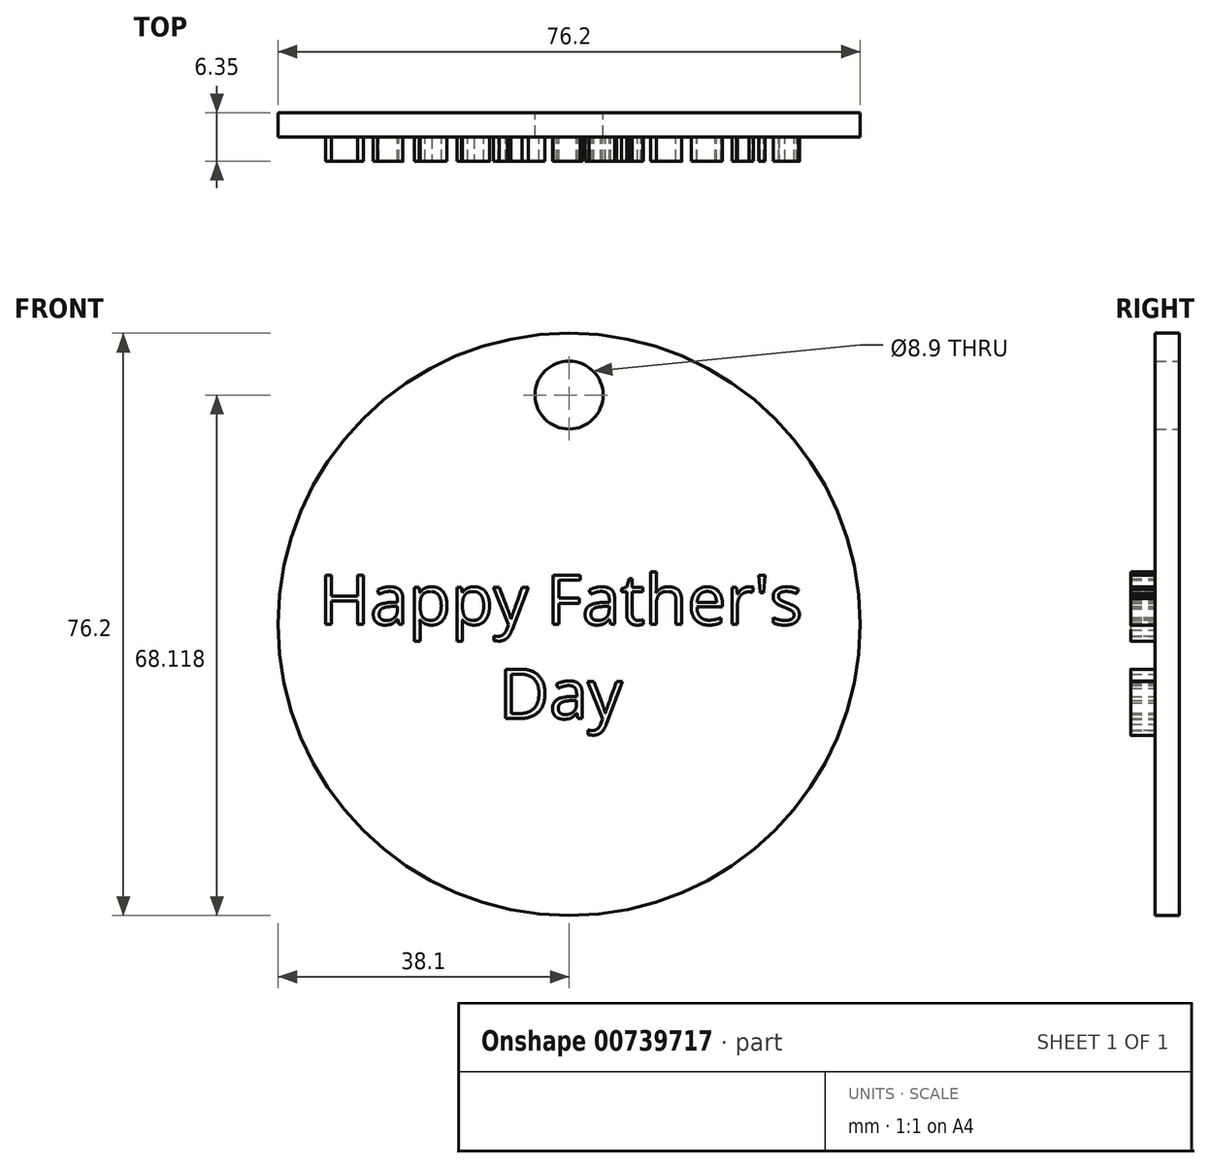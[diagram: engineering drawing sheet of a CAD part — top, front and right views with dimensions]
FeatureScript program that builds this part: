
annotation { "Feature Type Name" : "Feature", "Feature Type Description" : "" }
export const myFeature = defineFeature(function(context is Context, id is Id, definition is map)
    precondition{}
    {
        {
            var Q0;
            Q0=qCreatedBy(makeId("Front.planeOp"),FACE);
            var sketch = newSketch(context, id + "F0", { "sketchPlane" : qUnion([Q0])});
            skCircle(sketch, "E0", {"center": v(0, 0) * mm, "radius": 38.1 * mm});
            skSolve(sketch);
        }
        {
            var Q0;
            Q0 = qSketchRegion(id + "F0", true);
            extrude(context, id + "F1", {"entities" : qUnion([Q0]), "depth" : 3.17 * mm, "offsetDistance" : 25.4 * mm});
        }
        {
            var Q0;
            Q0=makeQuery(id+"F1.opExtrude","CAP_FACE",FACE,{"disambiguationData":[OSD([sQuery(id+"F0.wireOp",EDGE,"E0")])],"isStart":false});
            var sketch = newSketch(context, id + "F2", { "sketchPlane" : qUnion([Q0])});
            skText(sketch, "E1", { "text": "Happy Father\'s\n          Day", "fontName": "OpenSans-Regular.ttf"});
            const initialGuessF2  = {"E1": [-0.03273, 0, 1, 0, 0.00652]};
            skSetInitialGuess(sketch, initialGuessF2);
            skSolve(sketch);
        }
        {
            var Q0;
            Q0 = qSketchRegion(id + "F2", true);
            extrude(context, id + "F3", {"entities" : qUnion([Q0]), "operationType" : NewBodyOperationType.ADD, "depth" : 3.17 * mm, "offsetDistance" : 25.4 * mm});
        }
        {
            var Q0;
            {var subQ0=sQuery(id+"F0.wireOp",EDGE,"E0");Q0=makeQuery(id+"F3.boolean.opBoolean","SPLIT",FACE,{"disambiguationData":[TD([makeQuery(id+"F1.opExtrude","SWEPT_FACE",FACE,{"disambiguationData":[OSD([subQ0])]})])],"derivedFrom":makeQuery(id+"F1.opExtrude","CAP_FACE",FACE,{"disambiguationData":[OSD([subQ0])],"isStart":false})});}
            var sketch = newSketch(context, id + "F4", { "sketchPlane" : qUnion([Q0])});
            skCircle(sketch, "E2", {"center": v(0, 30.02) * mm, "radius": 4.45 * mm});
            skSolve(sketch);
        }
        {
            var Q0;
            Q0 = qSketchRegion(id + "F4", true);
            extrude(context, id + "F5", {"entities" : qUnion([Q0]), "operationType" : NewBodyOperationType.REMOVE, "endBound" : BoundingType.SYMMETRIC, "depth" : 25.4 * mm, "offsetDistance" : 25.4 * mm});
        }
    });
